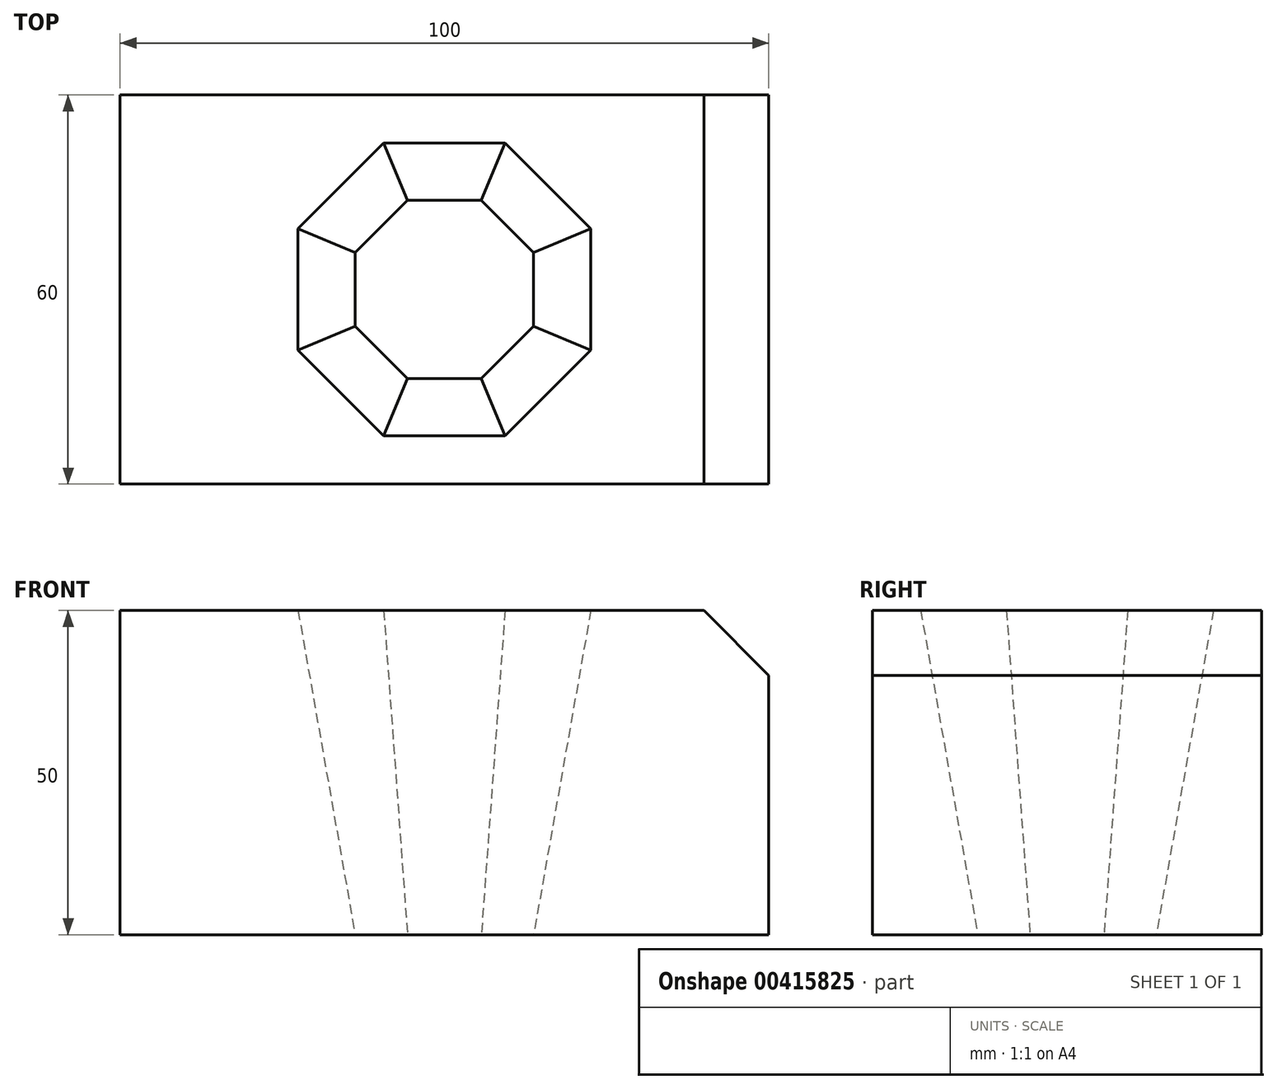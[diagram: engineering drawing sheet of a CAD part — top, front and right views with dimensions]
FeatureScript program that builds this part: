
annotation { "Feature Type Name" : "Feature", "Feature Type Description" : "" }
export const myFeature = defineFeature(function(context is Context, id is Id, definition is map)
    precondition{}
    {
        {
            var Q0;
            Q0=qCreatedBy(makeId("Top.planeOp"),FACE);
            var sketch = newSketch(context, id + "F0", { "sketchPlane" : qUnion([Q0])});
            skLineSegment(sketch, "E0.bottom", {"start": v(-50, 30) * mm, "end": v(50, 30) * mm});
            skLineSegment(sketch, "E0.top", {"start": v(-50, -30) * mm, "end": v(50, -30) * mm});
            skLineSegment(sketch, "E0.left", {"start": v(-50, 30) * mm, "end": v(-50, -30) * mm});
            skLineSegment(sketch, "E0.right", {"start": v(50, 30) * mm, "end": v(50, -30) * mm});
            skPoint(sketch, "E0.middle", {"position": v(0, 0) * mm});
            skSolve(sketch);
        }
        {
            var Q0;
            Q0=makeQuery(id+"F0.imprint","IMPRINT",FACE,{"disambiguationData":[TD([[makeQuery(id+"F0.imprint","IMPRINT",EDGE,{"derivedFrom":sQuery(id+"F0.wireOp",EDGE,"E0.bottom")}),-1.0]])]});
            extrude(context, id + "F1", {"entities" : qUnion([Q0]), "depth" : 50 * mm});
        }
        {
            var Q0;
            Q0=makeQuery(id+"F1.opExtrude","CAP_FACE",FACE,{"disambiguationData":[OSD([sQuery(id+"F0.wireOp",EDGE,"E0.bottom"),sQuery(id+"F0.wireOp",EDGE,"E0.top"),sQuery(id+"F0.wireOp",EDGE,"E0.left"),sQuery(id+"F0.wireOp",EDGE,"E0.right")])],"isStart":false});
            var sketch = newSketch(context, id + "F2", { "sketchPlane" : qUnion([Q0])});
            skCircle(sketch, "E1.cCircle", {"center": v(0, 0) * mm, "radius": 22.57 * mm, "construction": true});
            skLineSegment(sketch, "E1.0", {"start": v(-9.35, 22.57) * mm, "end": v(9.35, 22.57) * mm});
            skLineSegment(sketch, "E1.1", {"start": v(9.35, 22.57) * mm, "end": v(22.57, 9.35) * mm});
            skLineSegment(sketch, "E1.2", {"start": v(22.57, 9.35) * mm, "end": v(22.57, -9.35) * mm});
            skLineSegment(sketch, "E1.3", {"start": v(22.57, -9.35) * mm, "end": v(9.35, -22.57) * mm});
            skLineSegment(sketch, "E1.4", {"start": v(9.35, -22.57) * mm, "end": v(-9.35, -22.57) * mm});
            skLineSegment(sketch, "E1.5", {"start": v(-9.35, -22.57) * mm, "end": v(-22.57, -9.35) * mm});
            skLineSegment(sketch, "E1.6", {"start": v(-22.57, -9.35) * mm, "end": v(-22.57, 9.35) * mm});
            skLineSegment(sketch, "E1.7", {"start": v(-22.57, 9.35) * mm, "end": v(-9.35, 22.57) * mm});
            skPoint(sketch, "E1.0.midPoint", {"position": v(0, 22.57) * mm});
            skSolve(sketch);
        }
        {
            var Q0;
            Q0=makeQuery(id+"F1.opExtrude","CAP_FACE",FACE,{"disambiguationData":[OSD([sQuery(id+"F0.wireOp",EDGE,"E0.bottom"),sQuery(id+"F0.wireOp",EDGE,"E0.top"),sQuery(id+"F0.wireOp",EDGE,"E0.left"),sQuery(id+"F0.wireOp",EDGE,"E0.right")])],"isStart":true});
            var sketch = newSketch(context, id + "F3", { "sketchPlane" : qUnion([Q0])});
            skCircle(sketch, "E2.cCircle", {"center": v(0, 0) * mm, "radius": 13.75 * mm, "construction": true});
            skLineSegment(sketch, "E2.0", {"start": v(-13.75, -5.7) * mm, "end": v(-13.75, 5.7) * mm});
            skLineSegment(sketch, "E2.1", {"start": v(-13.75, 5.7) * mm, "end": v(-5.7, 13.75) * mm});
            skLineSegment(sketch, "E2.2", {"start": v(-5.7, 13.75) * mm, "end": v(5.7, 13.75) * mm});
            skLineSegment(sketch, "E2.3", {"start": v(5.7, 13.75) * mm, "end": v(13.75, 5.7) * mm});
            skLineSegment(sketch, "E2.4", {"start": v(13.75, 5.7) * mm, "end": v(13.75, -5.7) * mm});
            skLineSegment(sketch, "E2.5", {"start": v(13.75, -5.7) * mm, "end": v(5.7, -13.75) * mm});
            skLineSegment(sketch, "E2.6", {"start": v(5.7, -13.75) * mm, "end": v(-5.7, -13.75) * mm});
            skLineSegment(sketch, "E2.7", {"start": v(-5.7, -13.75) * mm, "end": v(-13.75, -5.7) * mm});
            skPoint(sketch, "E2.0.midPoint", {"position": v(-13.75, 0) * mm});
            skSolve(sketch);
        }
        {
            var Q1;
            Q1=makeQuery(id+"F2.imprint","IMPRINT",FACE,{"disambiguationData":[TD([[makeQuery(id+"F2.imprint","IMPRINT",EDGE,{"derivedFrom":sQuery(id+"F2.wireOp",EDGE,"E1.0")}),-1.0]])]});
            var Q2;
            Q2=makeQuery(id+"F3.imprint","IMPRINT",FACE,{"disambiguationData":[TD([[makeQuery(id+"F3.imprint","IMPRINT",EDGE,{"derivedFrom":sQuery(id+"F3.wireOp",EDGE,"E2.0")}),-1.0]])]});
            loft(context, id + "F4", {"operationType" : NewBodyOperationType.REMOVE, "sheetProfilesArray" : [{ "sheetProfileEntities" : qUnion([Q1]) }, { "sheetProfileEntities" : qUnion([Q2]) }]});
        }
        {
            var Q0;
            Q0=makeQuery(id+"F1.opExtrude","CAP_EDGE",EDGE,{"disambiguationData":[OSD([sQuery(id+"F0.wireOp",EDGE,"E0.right")])],"isStart":false});
            chamfer(context, id + "F5", {"entities" : qUnion([Q0]), "width" : 10 * mm, "tangentPropagation" : true});
        }
    });
